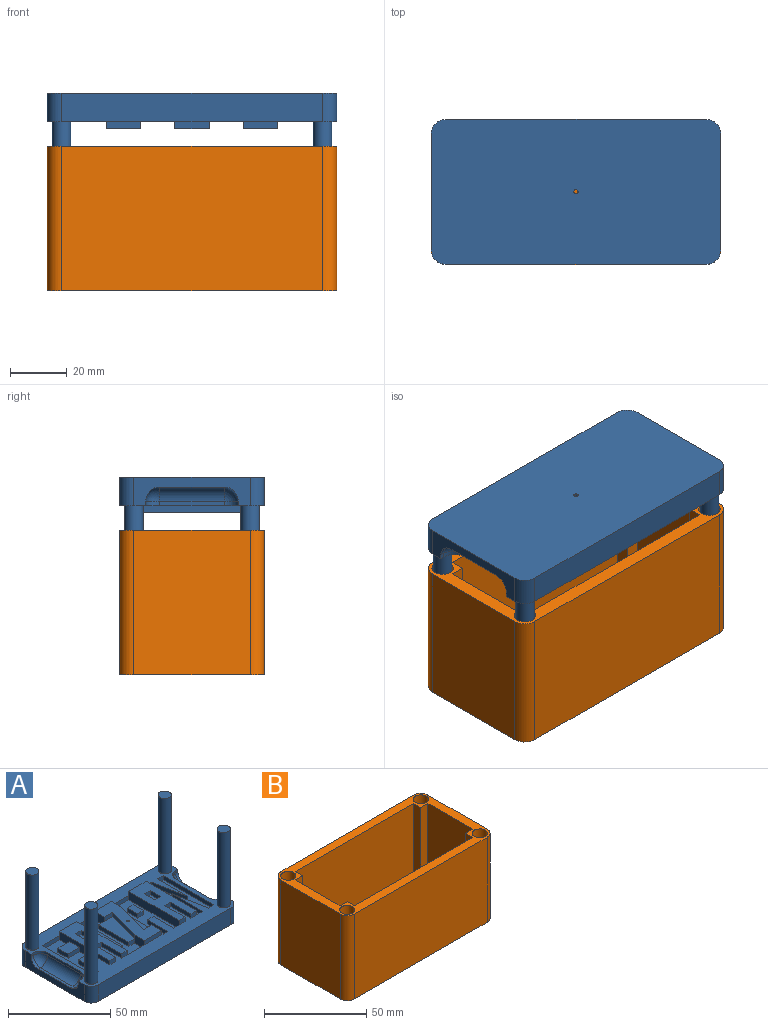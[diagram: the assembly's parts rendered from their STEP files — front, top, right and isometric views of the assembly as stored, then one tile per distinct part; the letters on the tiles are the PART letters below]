
ASSEMBLY  parts=2 mates=1
PART A: 123 faces, bbox 101.6x50.8x55 mm
  f0: plane 101.6x50.8mm, normal (0,0,1), area 2030mm2, adj f5,f6,f7,f8,f9,f10,f11,f13
  f1: plane 21x10mm, normal (0,0,1), area 147mm2, adj f74,f75,f76,f107,f108
  f2: plane 21x6mm, normal (0,0,1), area 63mm2, adj f57,f104,f105
  f3: plane 8x7mm, normal (0,0,1), area 56mm2, adj f82,f83,f89,f90
  f4: plane 21x4mm, normal (0,0,1), area 84mm2, adj f70,f71,f79,f80
  f5: plane 91.6x10mm, normal (0,1,0), area 916mm2, adj f0,f6,f13,f14
  f6: cylinder r=5mm len=10mm, axis (0,0,-1), area 78.5mm2, adj f0,f5,f7,f14
  f7: plane 40.8x10mm, normal (-1,0,0), area 207.5mm2, adj f0,f6,f8,f14,f34,f35,f36,f37
  f8: cylinder r=5mm len=10mm, axis (0,0,-1), area 78.5mm2, adj f0,f7,f9,f14
  f9: plane 91.6x10mm, normal (0,-1,0), area 916mm2, adj f0,f8,f10,f14
  f10: cylinder r=5mm len=10mm, axis (0,0,-1), area 78.5mm2, adj f0,f9,f11,f14
  f11: plane 40.8x10mm, normal (1,0,0), area 207.5mm2, adj f0,f10,f13,f14,f23,f24,f25,f26
  f12: cylinder r=0.75mm len=12.5mm, axis (0,0,-1), area 58.9mm2, adj f14,f110
  f13: cylinder r=5mm len=10mm, axis (0,0,-1), area 78.5mm2, adj f0,f5,f11,f14
  f14: plane 101.6x50.8mm, normal (0,0,-1), area 5138.1mm2, adj f5,f6,f7,f8,f9,f10,f11,f12
  f15: cylinder r=3.25mm len=45mm, axis (0,0,-1), area 918.9mm2, adj f0,f16
  f16: plane 6.5x6.5mm, normal (0,0,1), area 33.2mm2, adj f15
  f17: cylinder r=3.25mm len=45mm, axis (0,0,-1), area 918.9mm2, adj f0,f18
  f18: plane 6.5x6.5mm, normal (0,0,1), area 33.2mm2, adj f17
  f19: cylinder r=3.25mm len=45mm, axis (0,0,-1), area 918.9mm2, adj f0,f20
  f20: plane 6.5x6.5mm, normal (0,0,1), area 33.2mm2, adj f19
  f21: cylinder r=3.25mm len=45mm, axis (0,0,-1), area 918.9mm2, adj f0,f22
  f22: plane 6.5x6.5mm, normal (0,0,1), area 33.2mm2, adj f21
  f23: plane 1.5x1.5mm, normal (0,-1,0), area 2.2mm2, adj f0,f11,f27,f33
  f24: plane 1.5x1.5mm, normal (0,1,0), area 2.2mm2, adj f0,f11,f25,f29
  f25: cylinder r=5mm len=5mm, axis (1,0,0), area 11.8mm2, adj f11,f24,f26,f30
  f26: plane 22.5x1.5mm, normal (0,0,1), area 33.7mm2, adj f11,f25,f27,f31
  f27: cylinder r=5mm len=5mm, axis (1,0,0), area 11.8mm2, adj f11,f23,f26,f32
  f28: plane 22.5x1.5mm, normal (1,0,0), area 33.8mm2, adj f0,f29,f31,f33
  f29: cylinder r=5mm len=5mm, axis (0,0,-1), area 11.8mm2, adj f0,f24,f28,f30
  f30: sphere r=5mm, area 39.3mm2, adj f25,f29,f31
  f31: cylinder r=5mm len=22.5mm, axis (0,1,0), area 176.7mm2, adj f26,f28,f30,f32
  f32: sphere r=5mm, area 39.3mm2, adj f27,f31,f33
  f33: cylinder r=5mm len=5mm, axis (0,0,1), area 11.8mm2, adj f0,f23,f28,f32
  f34: plane 1.5x1.5mm, normal (0,-1,0), area 2.3mm2, adj f0,f7,f35,f44
  f35: cylinder r=5mm len=5mm, axis (-1,0,0), area 11.8mm2, adj f7,f34,f36,f43
  f36: plane 22.5x1.5mm, normal (0,0,1), area 33.8mm2, adj f7,f35,f37,f42
  f37: cylinder r=5mm len=5mm, axis (-1,0,0), area 11.8mm2, adj f7,f36,f38,f41
  f38: plane 1.5x1.5mm, normal (0,1,0), area 2.3mm2, adj f0,f7,f37,f40
  f39: plane 22.5x1.5mm, normal (-1,0,0), area 33.7mm2, adj f0,f40,f42,f44
  f40: cylinder r=5mm len=5mm, axis (0,0,1), area 11.8mm2, adj f0,f38,f39,f41
  f41: sphere r=5mm, area 39.3mm2, adj f37,f40,f42
  f42: cylinder r=5mm len=22.5mm, axis (0,-1,0), area 176.7mm2, adj f36,f39,f41,f43
  f43: sphere r=5mm, area 39.3mm2, adj f35,f42,f44
  f44: cylinder r=5mm len=5mm, axis (0,0,-1), area 11.8mm2, adj f0,f34,f39,f43
  f45: plane 35x5mm, normal (1,0,0), area 175mm2, adj f46,f54,f55,f111,f116,f121
  f46: plane 4x2.5mm, normal (0,1,0), area 10mm2, adj f0,f45,f47,f55
  f47: plane 21x2.5mm, normal (-1,0,0), area 52.5mm2, adj f0,f46,f48,f55
  f48: plane 21x4mm, normal (0.98,0.19,0), area 53.4mm2, adj f0,f47,f49,f55
  f49: plane 4x2.5mm, normal (0,1,0), area 10mm2, adj f0,f48,f50,f55
  f50: plane 35x2.5mm, normal (-1,0,0), area 87.5mm2, adj f0,f49,f51,f55
  f51: plane 4x2.5mm, normal (0,-1,0), area 10mm2, adj f0,f50,f52,f55
  f52: plane 21x2.5mm, normal (1,0,0), area 52.5mm2, adj f0,f51,f53,f55
  f53: plane 21x4mm, normal (-0.98,-0.19,0), area 53.4mm2, adj f0,f52,f54,f55
  f54: plane 4x2.5mm, normal (0,-1,0), area 10mm2, adj f0,f45,f53,f55
  f55: plane 35x12mm, normal (0,0,1), area 336mm2, adj f45,f46,f47,f48,f49,f50,f51,f52
  f56: plane 12x2.5mm, normal (0,-1,0), area 30mm2, adj f0,f57,f67,f68
  f57: plane 35x5mm, normal (1,0,0), area 122.5mm2, adj f2,f56,f58,f68,f104,f105,f106,f109
  f58: plane 4x2.5mm, normal (0,1,0), area 10mm2, adj f0,f57,f59,f68
  f59: plane 14x2.5mm, normal (-1,0,0), area 35mm2, adj f0,f58,f60,f68
  f60: plane 4x2.5mm, normal (0,1,0), area 10mm2, adj f0,f59,f61,f68
  f61: plane 14x2.5mm, normal (1,0,0), area 35mm2, adj f0,f60,f62,f68
  f62: plane 4x2.5mm, normal (0,1,0), area 10mm2, adj f0,f61,f67,f68
  f63: plane 4x2.5mm, normal (0,1,0), area 10mm2, adj f64,f66,f68,f69
  f64: plane 7x2.5mm, normal (1,0,0), area 17.5mm2, adj f63,f65,f68,f69
  f65: plane 4x2.5mm, normal (0,-1,0), area 10mm2, adj f64,f66,f68,f69
  f66: plane 7x2.5mm, normal (-1,0,0), area 17.5mm2, adj f63,f65,f68,f69
  f67: plane 35x5mm, normal (-1,0,0), area 175mm2, adj f56,f62,f68,f111,f112,f121
  f68: plane 35x12mm, normal (0,0,1), area 336mm2, adj f56,f57,f58,f59,f60,f61,f62,f63
  f69: plane 7x4mm, normal (0,0,1), area 28mm2, adj f63,f64,f65,f66
  f70: plane 4x2.5mm, normal (0,-1,0), area 10mm2, adj f4,f71,f80,f81
  f71: plane 35x5mm, normal (1,0,0), area 122.5mm2, adj f4,f70,f72,f78,f79,f81,f93,f94
  f72: plane 12x2.5mm, normal (0,1,0), area 30mm2, adj f0,f71,f73,f81
  f73: plane 7x5mm, normal (-1,0,0), area 35mm2, adj f72,f74,f81,f108,f109,f110
  f74: plane 4x2.5mm, normal (0,-1,0), area 10mm2, adj f1,f73,f75,f81
  f75: plane 21x2.5mm, normal (-1,0,0), area 52.5mm2, adj f1,f74,f76,f81
  f76: plane 4x2.5mm, normal (0,1,0), area 10mm2, adj f1,f75,f77,f81
  f77: plane 7x5mm, normal (-1,0,0), area 35mm2, adj f76,f78,f81,f106,f107,f110
  f78: plane 12x2.5mm, normal (0,-1,0), area 30mm2, adj f0,f71,f77,f81
  f79: plane 4x2.5mm, normal (0,1,0), area 10mm2, adj f4,f71,f80,f81
  f80: plane 21x2.5mm, normal (1,0,0), area 52.5mm2, adj f4,f70,f79,f81
  f81: plane 35x12mm, normal (0,0,1), area 252mm2, adj f70,f71,f72,f73,f74,f75,f76,f77
  f82: plane 8x2.5mm, normal (0,1,0), area 20mm2, adj f3,f83,f90,f91
  f83: plane 35x5mm, normal (-1,0,0), area 122.5mm2, adj f0,f3,f82,f84,f88,f89,f91,f94
  f84: plane 12x2.5mm, normal (0,-1,0), area 30mm2, adj f0,f83,f85,f91
  f85: plane 35x2.5mm, normal (1,0,0), area 87.5mm2, adj f0,f84,f86,f91
  f86: plane 4x2.5mm, normal (0,1,0), area 10mm2, adj f0,f85,f87,f91
  f87: plane 14x2.5mm, normal (-1,0,0), area 35mm2, adj f0,f86,f88,f91
  f88: plane 8x2.5mm, normal (0,1,0), area 20mm2, adj f0,f83,f87,f91
  f89: plane 8x2.5mm, normal (0,-1,0), area 20mm2, adj f3,f83,f90,f91
  f90: plane 7x2.5mm, normal (-1,0,0), area 17.5mm2, adj f3,f82,f89,f91
  f91: plane 35x12mm, normal (0,0,1), area 252mm2, adj f82,f83,f84,f85,f86,f87,f88,f89
  f92: plane 14x2.5mm, normal (-1,0,0), area 35mm2, adj f0,f93,f101,f102
  f93: plane 4x2.5mm, normal (0,-1,0), area 10mm2, adj f0,f71,f92,f102
  f94: plane 12x2.5mm, normal (0,1,0), area 30mm2, adj f0,f71,f83,f102
  f95: plane 4x2.5mm, normal (0,-1,0), area 10mm2, adj f0,f83,f96,f102
  f96: plane 14x2.5mm, normal (1,0,0), area 35mm2, adj f0,f95,f101,f102
  f97: plane 7x2.5mm, normal (1,0,0), area 17.5mm2, adj f98,f100,f102,f103
  f98: plane 4x2.5mm, normal (0,-1,0), area 10mm2, adj f97,f99,f102,f103
  f99: plane 7x2.5mm, normal (-1,0,0), area 17.5mm2, adj f98,f100,f102,f103
  f100: plane 4x2.5mm, normal (0,1,0), area 10mm2, adj f97,f99,f102,f103
  f101: plane 4x2.5mm, normal (0,-1,0), area 10mm2, adj f0,f92,f96,f102
  f102: plane 35x12mm, normal (0,0,1), area 336mm2, adj f71,f83,f92,f93,f94,f95,f96,f97
  f103: plane 7x4mm, normal (0,0,1), area 28mm2, adj f97,f98,f99,f100
  f104: plane 6x2.5mm, normal (0,1,0), area 15mm2, adj f2,f57,f105,f110
  f105: plane 21x6mm, normal (0.96,-0.27,0), area 54.6mm2, adj f2,f57,f104,f110
  f106: plane 12x2.5mm, normal (0,1,0), area 30mm2, adj f0,f57,f77,f110
  f107: plane 6x2.5mm, normal (0,-1,0), area 15mm2, adj f1,f77,f108,f110
  f108: plane 21x6mm, normal (-0.96,0.27,0), area 54.6mm2, adj f1,f73,f107,f110
  f109: plane 12x2.5mm, normal (0,-1,0), area 30mm2, adj f0,f57,f73,f110
  f110: plane 35x12mm, normal (0,0,1), area 292.2mm2, adj f12,f57,f73,f77,f104,f105,f106,f107
  f111: plane 12x2.5mm, normal (0,1,0), area 30mm2, adj f0,f45,f67,f121
  f112: plane 4x2.5mm, normal (0,-1,0), area 10mm2, adj f0,f67,f113,f121
  f113: plane 14x2.5mm, normal (1,0,0), area 35mm2, adj f0,f112,f114,f121
  f114: plane 4x2.5mm, normal (0,-1,0), area 10mm2, adj f0,f113,f115,f121
  f115: plane 14x2.5mm, normal (-1,0,0), area 35mm2, adj f0,f114,f116,f121
  f116: plane 4x2.5mm, normal (0,-1,0), area 10mm2, adj f0,f45,f115,f121
  f117: plane 7x2.5mm, normal (1,0,0), area 17.5mm2, adj f118,f120,f121,f122
  f118: plane 4x2.5mm, normal (0,-1,0), area 10mm2, adj f117,f119,f121,f122
  f119: plane 7x2.5mm, normal (-1,0,0), area 17.5mm2, adj f118,f120,f121,f122
  f120: plane 4x2.5mm, normal (0,1,0), area 10mm2, adj f117,f119,f121,f122
  f121: plane 35x12mm, normal (0,0,1), area 336mm2, adj f45,f67,f111,f112,f113,f114,f115,f116
  f122: plane 7x4mm, normal (0,0,1), area 28mm2, adj f117,f118,f119,f120
PART B: 35 faces, bbox 101.6x50.8x50.8 mm
  f0: plane 91.6x40.8mm, normal (0,0,1), area 3637.3mm2, adj f1,f2,f3,f4,f15,f16,f17,f18
  f1: plane 45.8x30.8mm, normal (1,0,0), area 1410.6mm2, adj f0,f14,f19,f21
  f2: plane 81.6x45.8mm, normal (0,1,0), area 3737.3mm2, adj f0,f14,f18,f20
  f3: plane 45.8x30.8mm, normal (-1,0,0), area 1410.6mm2, adj f0,f14,f15,f17
  f4: plane 81.6x45.8mm, normal (0,-1,0), area 3737.3mm2, adj f0,f14,f16,f22
  f5: plane 91.6x50.8mm, normal (0,1,0), area 4653.3mm2, adj f6,f12,f13,f14
  f6: cylinder r=5mm len=50.8mm, axis (0,0,-1), area 399mm2, adj f5,f7,f13,f14
  f7: plane 50.8x40.8mm, normal (-1,0,0), area 2072.6mm2, adj f6,f8,f13,f14
  f8: cylinder r=5mm len=50.8mm, axis (0,0,-1), area 399mm2, adj f7,f9,f13,f14
  f9: plane 91.6x50.8mm, normal (0,-1,0), area 4653.3mm2, adj f8,f10,f13,f14
  f10: cylinder r=5mm len=50.8mm, axis (0,0,-1), area 399mm2, adj f9,f11,f13,f14
  f11: plane 50.8x40.8mm, normal (1,0,0), area 2072.6mm2, adj f10,f12,f13,f14
  f12: cylinder r=5mm len=50.8mm, axis (0,0,-1), area 399mm2, adj f5,f11,f13,f14
  f13: plane 101.6x50.8mm, normal (0,0,-1), area 5132.8mm2, adj f5,f6,f7,f8,f9,f10,f11,f12
  f14: plane 101.6x50.8mm, normal (0,0,1), area 1325.8mm2, adj f1,f2,f3,f4,f5,f6,f7,f8
  f15: plane 45.8x5mm, normal (0,-1,0), area 229mm2, adj f0,f3,f14,f16
  f16: plane 45.8x5mm, normal (-1,0,0), area 229mm2, adj f0,f4,f14,f15
  f17: plane 45.8x5mm, normal (0,1,0), area 229mm2, adj f0,f3,f14,f18
  f18: plane 45.8x5mm, normal (-1,0,0), area 229mm2, adj f0,f2,f14,f17
  f19: plane 45.8x5mm, normal (0,1,0), area 229mm2, adj f0,f1,f14,f20
  f20: plane 45.8x5mm, normal (1,0,0), area 229mm2, adj f0,f2,f14,f19
  f21: plane 45.8x5mm, normal (0,-1,0), area 229mm2, adj f0,f1,f14,f22
  f22: plane 45.8x5mm, normal (1,0,0), area 229mm2, adj f0,f4,f14,f21
  f23: cylinder r=3.75mm len=45mm, axis (0,0,1), area 1060.3mm2, adj f14,f24
  f24: plane 7.5x7.5mm, normal (0,0,1), area 42.4mm2, adj f23,f34
  f25: cylinder r=3.75mm len=45mm, axis (0,0,1), area 1060.3mm2, adj f14,f26
  f26: plane 7.5x7.5mm, normal (0,0,1), area 42.4mm2, adj f25,f33
  f27: cylinder r=3.75mm len=45mm, axis (0,0,1), area 1060.3mm2, adj f14,f28
  f28: plane 7.5x7.5mm, normal (0,0,1), area 42.4mm2, adj f27,f32
  f29: cylinder r=3.75mm len=45mm, axis (0,0,1), area 1060.3mm2, adj f14,f30
  f30: plane 7.5x7.5mm, normal (0,0,1), area 42.4mm2, adj f29,f31
  f31: cylinder r=0.75mm len=5.8mm, axis (0,0,1), area 27.3mm2, adj f13,f30
  f32: cylinder r=0.75mm len=5.8mm, axis (0,0,1), area 27.3mm2, adj f13,f28
  f33: cylinder r=0.75mm len=5.8mm, axis (0,0,1), area 27.3mm2, adj f13,f26
  f34: cylinder r=0.75mm len=5.8mm, axis (0,0,1), area 27.3mm2, adj f13,f24
PLACE A rot(axis=(1,0,0),180deg) t=(-288.08,186.84,-598.42)mm
PLACE B t=(-299.74,131.55,-667.88)mm
MATE slider B.f6 <-> A.f8  axis (0,0,1) through (-345.54,151.95,-617.08)mm
